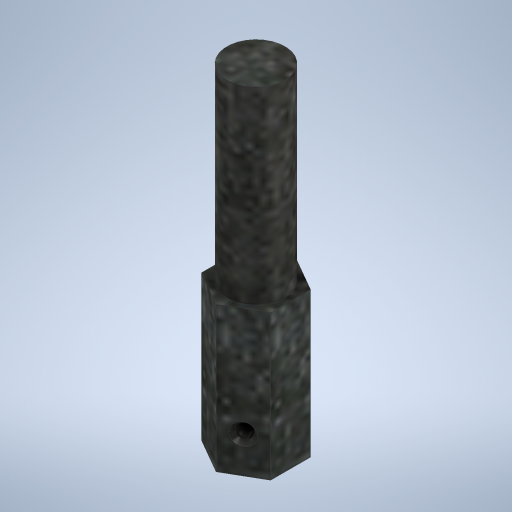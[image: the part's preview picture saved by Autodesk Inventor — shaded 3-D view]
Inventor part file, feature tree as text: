
AUTODESK INVENTOR PART (.ipt)
format: ipt  version: 2023 (Build 270158030, 158C)  size: 329,728 bytes
history: native  units: in
note: dims shown in document units (in); Inventor stores cm internally (conversion verified against a paired STEP export)
features: sketch x4, extrude x3, hole x1
ambient origin geometry x8: Origin, YZ Plane, XZ Plane, XY Plane, X Axis, Y Axis, Z Axis, Center Point
bodies: Solid1 (feature_tree)
feature tree (8):
  extrude  "Extrusion1"  Depth=0.7874in TaperAngle=0.0deg
  extrude  "Extrusion2"  Depth=0.1969in TaperAngle=0.0deg
  hole  "Hole1"  [1 undecoded]
  extrude  "Extrusion4"  Depth=0.1083in
  sketch  "Sketch1"  dims[d0=0.375in d1=0.7874in d2=0.0in]
  sketch  "Sketch2"  dims[d3=0.315in d4=0.1969in d5=0.0in]
  sketch  "Sketch4"  dims[d11=0.835in d12=0.0in d13=0.1969in]
  sketch  "Sketch5"  dims[d14=0.0787in d15=0.75in d16=0.1181in d17=0.25in d18=0.5635in d19=1.0in d20=0.8108in d21=0.1083in d22=0.8268in d23=0.0in]
note: 1 required parameter value undecoded (feature->parameter linkage not recoverable at this tier; creation-order binding heuristic only, values carry confidence <= 0.55)
